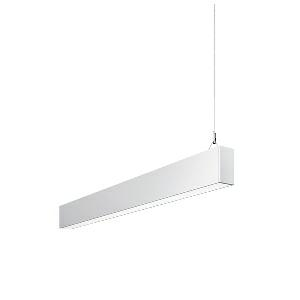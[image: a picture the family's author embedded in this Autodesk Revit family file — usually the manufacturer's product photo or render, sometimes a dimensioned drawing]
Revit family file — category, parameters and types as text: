
# Revit family: dotoo_line_-_dlp_2000_840_d_end_00805783_fc5d
name_source: partatom
category: Lighting Fixtures
units: mm (PartAtom-declared; Revit-internal decimal feet)

## family parameters
Cut with Voids When Loaded = No
Host = Face
Light Source = No
Part Type = Normal
Room Calculation Point = No
Round Connector Dimension = Use Diameter
Shared = No

## types (1)
- DOTOO.line - DLP 2000/840/D END (1 x LED, 1700 lm, 4000K)
    Apparent Load = 16 VA
    Approval mark = CE
    CIE Flux Codes = 67 91 98 100 100
    Color Rendering = 80-89
    Color Temperature = 4000K
    Control Gear = Electronic ballast
    Default Elevation = 1800 mm
    Description = DLP 2000/840/D|Suspended luminaire|light source: LED|connected load: 220-240 V, 50/60 Hz|Power consumption: approx. 16 W|standby: approx. 0,15|luminous flux: 1700 lm|luminous efficacy: 106 lm/W|light distribution: Direct|direct ratio: approx. 100 %|colour temperature: Cold white, ca. 4000 K|color rendering index (CRI): >= 80|chromaticity tolerance:  3 SDCM|System of protection: IP 40|technology: Continuously dimmable|luminaire body|material: Sectional aluminium|colour: White|lamp cover: Acrylic (PMMA), Clear|mains lead: 1,0 m With free stranded wires|Fastening: Steel cable 0.3 - 0.7 m|glare control: Prism aperture|luminance(L65): <= 3000 cd/m|unified glare rating(4H 8H): <=  19|special features: DALI Load 1x, TouchDIM - dimming via standard switch, Through-wired, up to 18 m on one mains connection, Flicker-free, Suitable as emergency lighting, Mechanical and electrical connection of the individual modules without tools|
    Frequency = 50 Hz
    Height = 110 mm
    Lamp = 1 x LED
    Lamp Light Flux = 1700 lm
    Lamp count = 1
    Length = 1408 mm
    Luminous efficacy = 106 lm/W
    Manufacturer = Waldmann
    ModVariant = No
    Model = 00805783
    Mounting Place = Ceiling
    Mounting Type = Pendant
    Number of Poles = 1
    OnlyDefault = Yes
    Power Factor = 1
    Product Name = DOTOO.line - DLP 2000/840/D END
    Product group = Suspended luminaire
    ProductGroupID = 9
    Protection Class = Protection class I
    Protection Degree = IP 40
    RLX_Detail_Level = 1
    RLX_Emergency_Light_Flux = 0 lm
    RLX_Emergency_Type = 0
    RLX_Emergency_Type_DB = No
    RlxData = <blob elided: 18357 chars, md5=5ff6414d>
    Socket = socket
    Standby Power = 0 W
    System Light Flux = 1700 lm
    System Power = 16 W
    Type Comments = Product without accessories
    Type Image = 113303000-00692573.jpg
    URL = http://relux.com
    VarID = ---
    Voltage = 230 V
    Voltage Range = 220-240 V
    Weight = 0.00 kg
    Width = 60 mm  [stored 0.19685 ft]

note: [stored X ft] marks values corroborated as IEEE doubles in the binary element streams (Revit-internal decimal feet)

## geometry (parser evidence)
native form markers: Blend x4, Sweep x13
no freeform markers — native parametric forms only
